# Revit family: CC4010001_Griferia teleducha Cascade
name_source: partatom
category: Plumbing Fixtures
units: mm (PartAtom-declared; Revit-internal decimal feet)

## family parameters
Always vertical = Yes
Cut with Voids When Loaded = No
OmniClass Number = 23.31.11.00
OmniClass Title = Faucets
Part Type = Normal
Room Calculation Point = No
Round Connector Dimension = Use Diameter
Shared = No
Work Plane-Based = No

## types (1)
- Teleducha Cascade
    Alto = 232 mm  [stored 0.761155 ft]
    Ancho = 102 mm
    Capacidad de flujo = A 80 psi: 9.3 L/min.
    Creado por = BIMBAU
    Default Elevation = 0 mm  [stored 0 ft]
    Description = La teleducha Cascade con tamaño medio y tecnología multiflow ofrece mayor relajación gracias a sus diferentes tipos de chorro, con selector de funciones tipo palanca para una fácil operación.
    Dimensiones generales producto (H * W * D) = 77 x 180 x 261 mm.
    Diámetro abasto = 13 mm
    Fecha de creación = 06/05/2021
    Garantía = 30 años - 2 años Acabados.
    Manufacturer = Corona.
    Material = Corona_Cromado
    Material 2 = Corona_Plastico_Gris
    Model = CC4010001_Griferia teleducha Cascade.
    Normatividad = NTC 1644.
    Peso neto = 410 g. - 0.9 lb.
    Presión máxima recomendada = 125 psi( 860 kPa).
    Presión mínima recomendada = 20 psi (140 kPa).
    Profundidad = 64 mm  [stored 0.209974 ft]
    Recubrimientos = Resistente a la corrosión, pelado y decoloración por agua. Recubrimientos no tóxicos. Producto para uso doméstico.
    Temperatura de uso = 5° C a 71° C.

note: [stored X ft] marks values corroborated as IEEE doubles in the binary element streams (Revit-internal decimal feet)

## geometry (parser evidence)
native form markers: Sweep x3
no freeform markers — native parametric forms only
